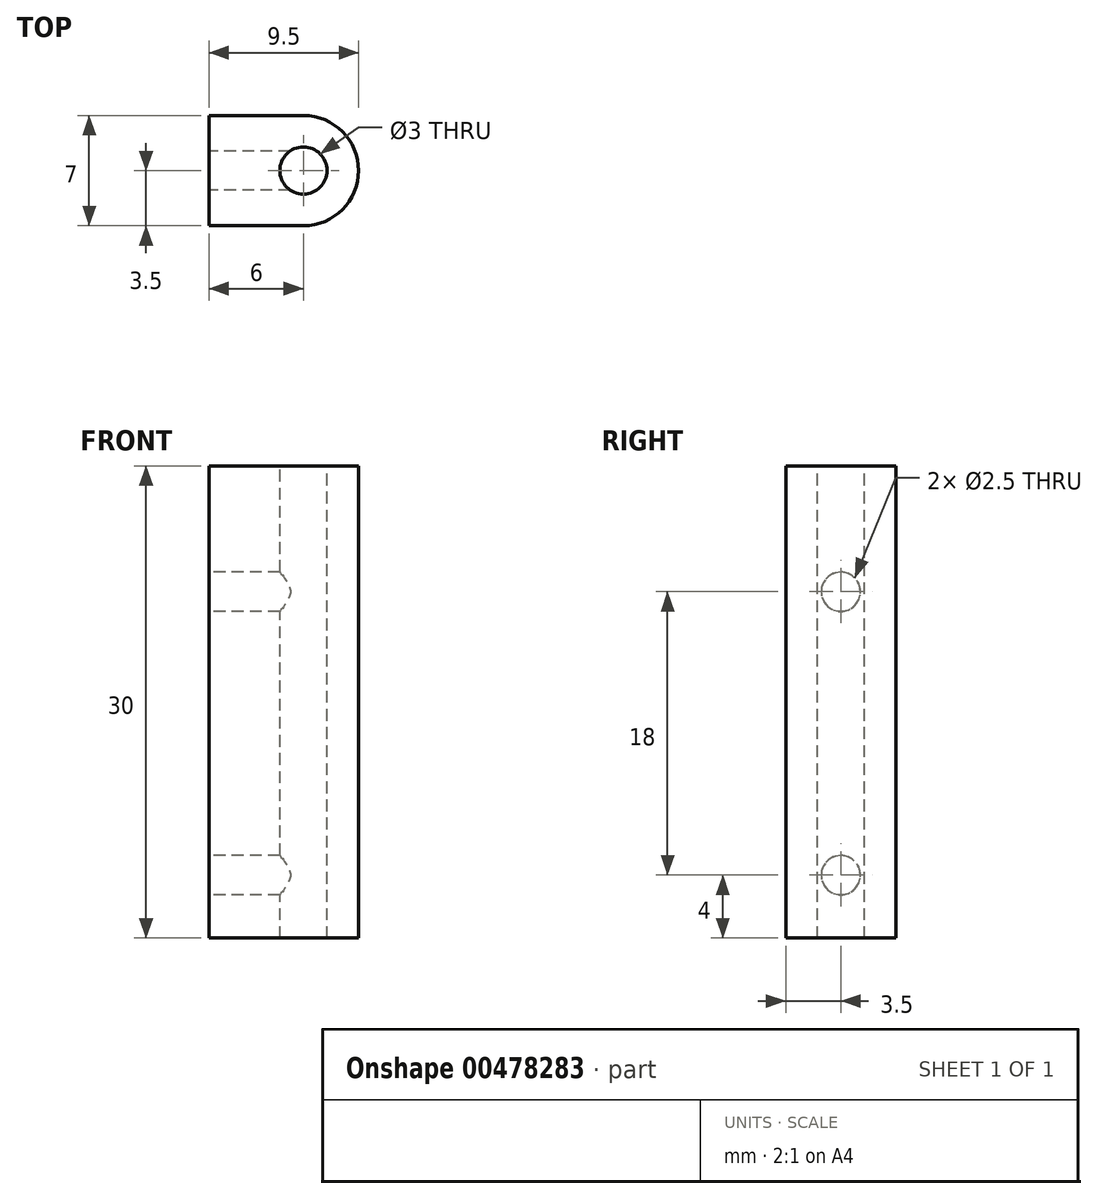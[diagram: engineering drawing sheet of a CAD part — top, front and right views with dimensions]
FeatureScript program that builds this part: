
annotation { "Feature Type Name" : "Feature", "Feature Type Description" : "" }
export const myFeature = defineFeature(function(context is Context, id is Id, definition is map)
    precondition{}
    {
        {
            var Q0;
            Q0=qCreatedBy(makeId("Top.planeOp"),FACE);
            var sketch = newSketch(context, id + "F0", { "sketchPlane" : qUnion([Q0])});
            skCircle(sketch, "E0", {"center": v(0, 0) * mm, "radius": 1.5 * mm});
            skCircle(sketch, "E1.0", {"center": v(0, 0) * mm, "radius": 3.5 * mm});
            skLineSegment(sketch, "E2", {"start": v(0, 3.5) * mm, "end": v(-6, 3.5) * mm});
            skLineSegment(sketch, "E3", {"start": v(-6, 3.5) * mm, "end": v(-6, -3.5) * mm});
            skLineSegment(sketch, "E4", {"start": v(-6, -3.5) * mm, "end": v(0, -3.5) * mm});
            skSolve(sketch);
        }
        {
            var Q0;
            {var subQ0=sQuery(id+"F0.wireOp",EDGE,"E2");Q0=makeQuery(id+"F0.imprint","IMPRINT",FACE,{"disambiguationData":[TD([[makeQuery(id+"F0.imprint","IMPRINT",EDGE,{"derivedFrom":subQ0}),1.0]])]});}
            var Q1;
            Q1=makeQuery(id+"F0.imprint","IMPRINT",FACE,{"disambiguationData":[TD([[makeQuery(id+"F0.imprint","IMPRINT",EDGE,{"derivedFrom":sQuery(id+"F0.wireOp",EDGE,"E0")}),-1.0]])]});
            extrude(context, id + "F1", {"entities" : qUnion([Q0, Q1]), "oppositeDirection" : true, "depth" : 30 * mm, "offsetDistance" : 25 * mm});
        }
        {
            var Q0;
            Q0=makeQuery(id+"F1.opExtrude","SWEPT_FACE",FACE,{"disambiguationData":[OSD([sQuery(id+"F0.wireOp",EDGE,"E3")])]});
            var sketch = newSketch(context, id + "F2", { "sketchPlane" : qUnion([Q0])});
            skPoint(sketch, "E5", {"position": v(0, -8) * mm});
            skLineSegment(sketch, "E6", {"start": v(-3.5, -15) * mm, "end": v(3.5, -15) * mm, "construction": true});
            skPoint(sketch, "E7.MirrorP", {"position": v(0, -26) * mm});
            skSolve(sketch);
        }
        {
            var Q0;
            Q0=sQuery(id+"F2.wireOp",VERTEX,"E7.MirrorP");
            var Q1;
            Q1=sQuery(id+"F2.wireOp",VERTEX,"E5");
            var Q2;
            Q2=makeQuery(id+"F1.opExtrude","SWEPT_BODY",BODY,{"disambiguationData":[OSD([sQuery(id+"F0.wireOp",EDGE,"E0"),sQuery(id+"F0.wireOp",EDGE,"E1.0"),sQuery(id+"F0.wireOp",EDGE,"E2"),sQuery(id+"F0.wireOp",EDGE,"E3"),sQuery(id+"F0.wireOp",EDGE,"E4")])]});
            hole(context, id + "F3", {"style" : HoleStyle.SIMPLE, "endStyle" : HoleEndStyle.BLIND, "holeDiameter" : 2.5 * mm, "holeDepth" : 6 * mm, "isTappedThrough" : true, "tappedDepth" : 12 * mm, "tapClearance" : 3, "locations" : qUnion([Q0, Q1]), "scope" : qUnion([Q2])});
        }
    });
